# Revit family: 913506000001(architecture=350)
name_source: partatom
category: Plumbing Fixtures
units: mm (PartAtom-declared; Revit-internal decimal feet)

## family parameters
Always vertical = Yes
Cut with Voids When Loaded = No
OmniClass Number = 23.31.13.11
Room Calculation Point = No
Shared = Yes
Work Plane-Based = No

## types (1)
- 913506000001(architecture=350)
    A = 913506000001
    ARTICLENO = NB
    B = parts/3188.png
    BOMINFO = LINA
    C = CAYONO - Bowl
    CATALOG = Kaldewei
    D = 11.00 kg
    Description = CAYONO Waschtisch-Schale
    E = KALDEWEI
    EF000003 = post top
    EF000007 = alpine white
    EF000040 = 151 mm  [stored 0.495407 ft]
    EF000049 = 355 mm
    EF000051 = Shape E
    EF002169 = steel enamel
    EF002442 = blade mounting
    EF004567 = 520 mm  [stored 1.70604 ft]
    F = 4055761222204
    G = 910700010999 (Modell 3917)
    H = not applicable
    I = https://www.kaldewei.de
    J = all countrys
    K = ISO 14025, EN 15804
    L = 30
    LINA = 913506000001(architecture=350)
    LODLEVEL = 350
    M = Furnishing Element
    MNR = 3188
    Manufacturer = Kaldewei
    Model = 913506000001(architecture=350)
    N = IfcSanitaryTerminalType Year
    NB = 913506000001(architecture=350)
    NBSYN = $A.($LODDEST.=$LODLEVEL.)
    NN = 3188
    NORM = CE certificate
    NT = CAYONO Waschtisch-Schale
    O = SS-35-65-70-94
    P = Wash Basin Systems
    Q = 23-31-13-11
    R = RVT_METRICPLUMBINGFIXTURE
    S = EC011550
    SUPPLIER = KALDEWEI
    etim7_EC011550 = EC011550
    etim7_EC011550_FORM = Rectangular
    etim7_EC011550_MONTAGEART = Post top
    ifc40_IFC4_IFCFURNISHINGELEMENT = IFC4_IFCFURNISHINGELEMENT

note: [stored X ft] marks values corroborated as IEEE doubles in the binary element streams (Revit-internal decimal feet)

## geometry (parser evidence)
native form markers: Sweep x10
no freeform markers — native parametric forms only
